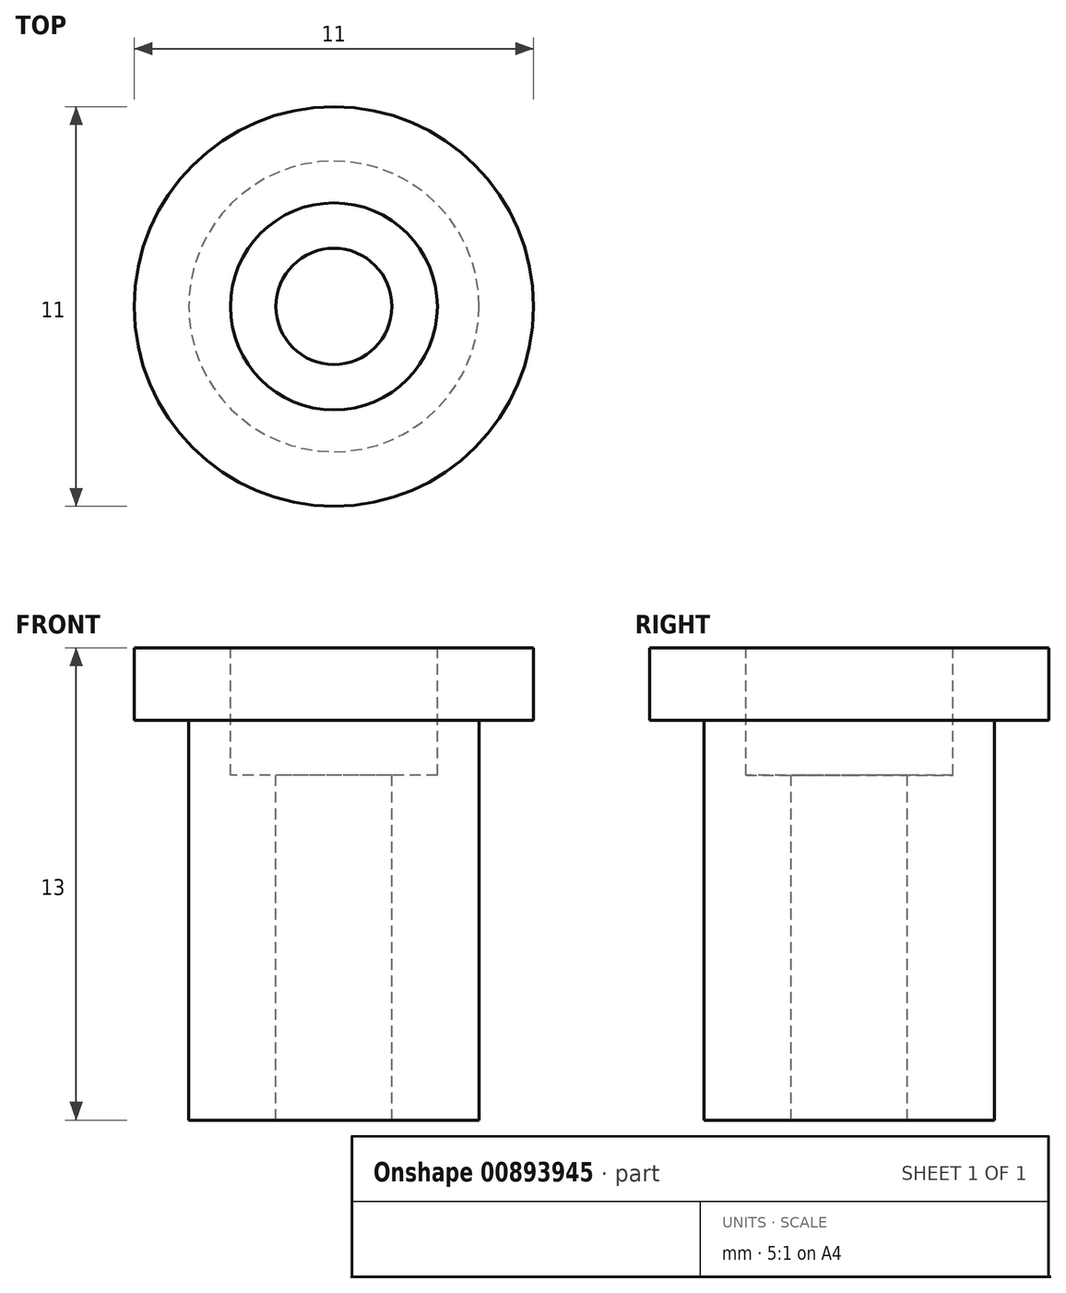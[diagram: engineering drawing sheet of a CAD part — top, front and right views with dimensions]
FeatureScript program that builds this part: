
annotation { "Feature Type Name" : "Feature", "Feature Type Description" : "" }
export const myFeature = defineFeature(function(context is Context, id is Id, definition is map)
    precondition{}
    {
        {
            var Q0;
            Q0=qCreatedBy(makeId("Top.planeOp"),FACE);
            var sketch = newSketch(context, id + "F0", { "sketchPlane" : qUnion([Q0])});
            skCircle(sketch, "E0", {"center": v(0, 0) * mm, "radius": 4 * mm});
            skSolve(sketch);
        }
        {
            var Q0;
            Q0 = qSketchRegion(id + "F0", true);
            extrude(context, id + "F1", {"entities" : qUnion([Q0]), "depth" : 11 * mm, "offsetDistance" : 25 * mm});
        }
        {
            var Q0;
            Q0=makeQuery(id+"F1.opExtrude","CAP_FACE",FACE,{"disambiguationData":[OSD([sQuery(id+"F0.wireOp",EDGE,"E0")])],"isStart":false});
            var sketch = newSketch(context, id + "F2", { "sketchPlane" : qUnion([Q0])});
            skCircle(sketch, "E1.0", {"center": v(0, 0) * mm, "radius": 5.5 * mm});
            skSolve(sketch);
        }
        {
            var Q0;
            Q0=makeQuery(id+"F2.imprint","IMPRINT",FACE,{"disambiguationData":[TD([[makeQuery(id+"F2.imprint","IMPRINT",EDGE,{"derivedFrom":makeQuery(id+"F1.opExtrude","CAP_EDGE",EDGE,{"disambiguationData":[OSD([sQuery(id+"F0.wireOp",EDGE,"E0")])],"isStart":false})}),1.0]])]});
            var Q1;
            Q1=makeQuery(id+"F2.imprint","IMPRINT",FACE,{"disambiguationData":[TD([[makeQuery(id+"F2.imprint","IMPRINT",EDGE,{"derivedFrom":sQuery(id+"F2.wireOp",EDGE,"E1.0")}),1.0]])]});
            extrude(context, id + "F3", {"entities" : qUnion([Q0, Q1]), "operationType" : NewBodyOperationType.ADD, "depth" : 2 * mm, "offsetDistance" : 25 * mm});
        }
        {
            var Q0;
            Q0=makeQuery(id+"F3.opExtrude","CAP_FACE",FACE,{"disambiguationData":[OSD([sQuery(id+"F2.wireOp",EDGE,"E1.0")])],"isStart":false});
            var sketch = newSketch(context, id + "F4", { "sketchPlane" : qUnion([Q0])});
            skLineSegment(sketch, "E2", {"start": v(0, 5.5) * mm, "end": v(0, -5.5) * mm, "construction": true});
            skLineSegment(sketch, "E3", {"start": v(5.5, 0) * mm, "end": v(-5.5, 0) * mm, "construction": true});
            skCircle(sketch, "E4", {"center": v(0, 0) * mm, "radius": 2.85 * mm});
            skSolve(sketch);
        }
        {
            var Q0;
            Q0 = qSketchRegion(id + "F4", true);
            extrude(context, id + "F5", {"entities" : qUnion([Q0]), "operationType" : NewBodyOperationType.REMOVE, "oppositeDirection" : true, "depth" : 3.5 * mm, "offsetDistance" : 25 * mm});
        }
        {
            var Q0;
            Q0=makeQuery(id+"F5.boolean.opBoolean","COPY",FACE,{"derivedFrom":makeQuery(id+"F5.opExtrude","CAP_FACE",FACE,{"disambiguationData":[OSD([sQuery(id+"F4.wireOp",EDGE,"E4")])],"isStart":false})});
            var sketch = newSketch(context, id + "F6", { "sketchPlane" : qUnion([Q0])});
            skLineSegment(sketch, "E5", {"start": v(0, -2.85) * mm, "end": v(0, 2.85) * mm, "construction": true});
            skLineSegment(sketch, "E6", {"start": v(2.85, 0) * mm, "end": v(-2.85, 0) * mm, "construction": true});
            skCircle(sketch, "E7", {"center": v(0, 0) * mm, "radius": 1.6 * mm});
            skSolve(sketch);
        }
        {
            var Q0;
            Q0 = qSketchRegion(id + "F6", true);
            extrude(context, id + "F7", {"entities" : qUnion([Q0]), "operationType" : NewBodyOperationType.REMOVE, "oppositeDirection" : true, "depth" : 25 * mm, "offsetDistance" : 25 * mm});
        }
    });
